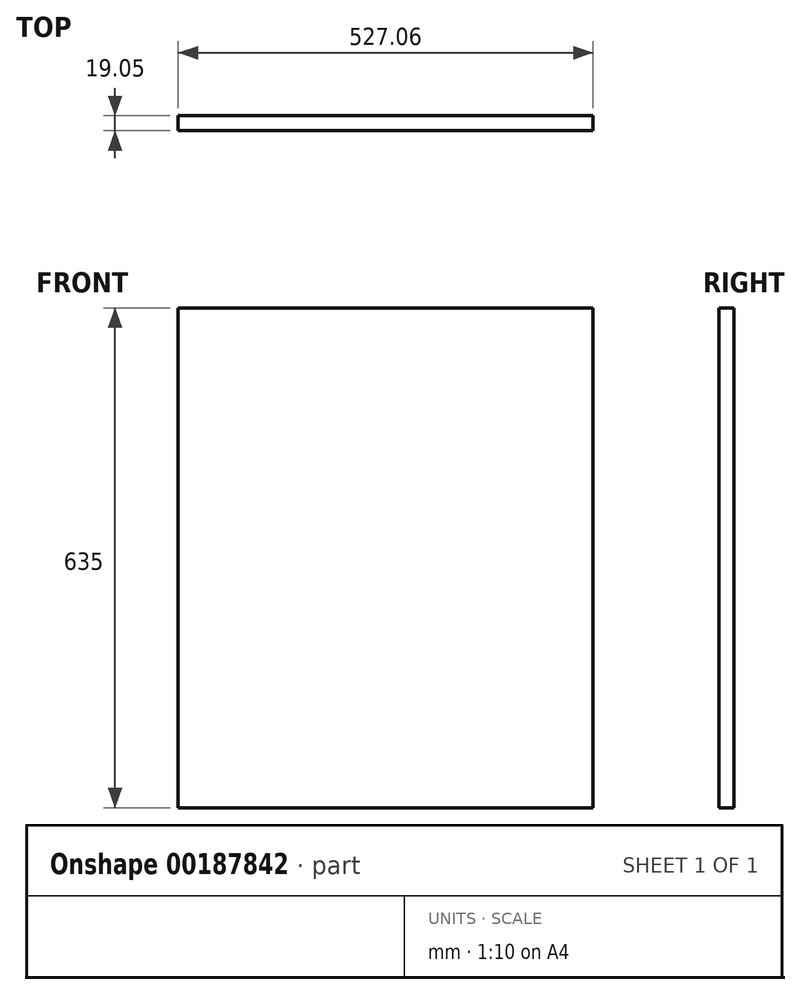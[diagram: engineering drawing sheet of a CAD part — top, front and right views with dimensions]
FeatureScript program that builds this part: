
annotation { "Feature Type Name" : "Feature", "Feature Type Description" : "" }
export const myFeature = defineFeature(function(context is Context, id is Id, definition is map)
    precondition{}
    {
        {
            var Q0;
            Q0=qCreatedBy(makeId("Front.planeOp"),FACE);
            var sketch = newSketch(context, id + "F0", { "sketchPlane" : qUnion([Q0])});
            skLineSegment(sketch, "E0.bottom", {"start": v(-263.52, 317.5) * mm, "end": v(263.53, 317.5) * mm});
            skLineSegment(sketch, "E0.top", {"start": v(-263.53, -317.5) * mm, "end": v(263.52, -317.5) * mm});
            skLineSegment(sketch, "E0.left", {"start": v(-263.52, 317.5) * mm, "end": v(-263.53, -317.5) * mm});
            skLineSegment(sketch, "E0.right", {"start": v(263.53, 317.5) * mm, "end": v(263.52, -317.5) * mm});
            skPoint(sketch, "E0.middle", {"position": v(0, 0) * mm});
            skSolve(sketch);
        }
        {
            var Q0;
            Q0=makeQuery(id+"F0.imprint","IMPRINT",FACE,{"disambiguationData":[TD([[makeQuery(id+"F0.imprint","IMPRINT",EDGE,{"derivedFrom":sQuery(id+"F0.wireOp",EDGE,"E0.bottom")}),-1.0]])]});
            extrude(context, id + "F1", {"entities" : qUnion([Q0]), "depth" : 19.05 * mm});
        }
    });
